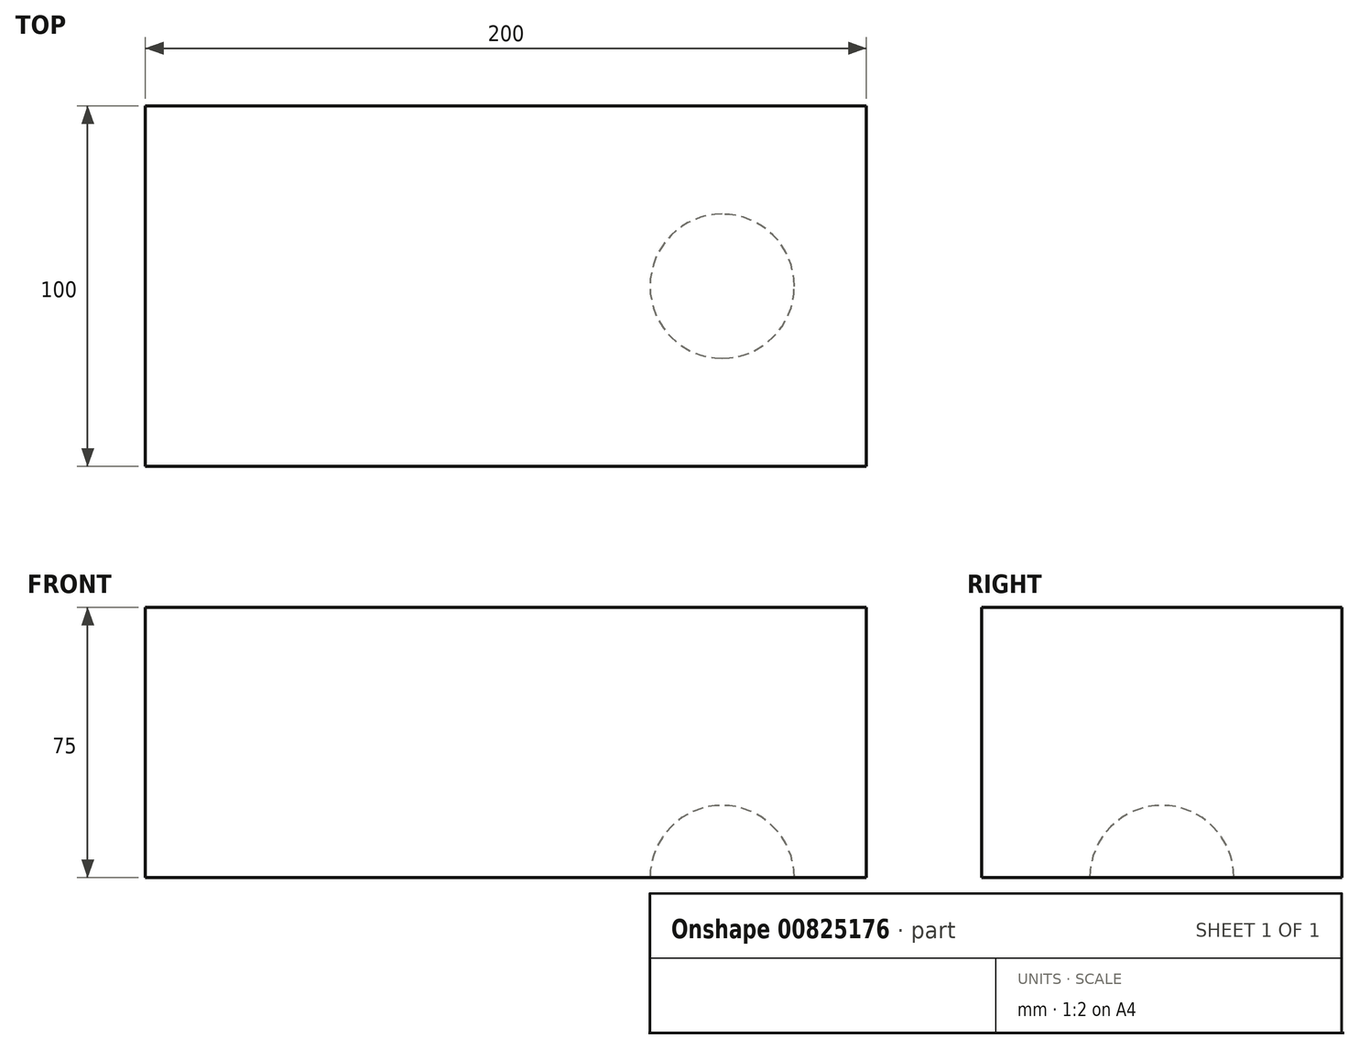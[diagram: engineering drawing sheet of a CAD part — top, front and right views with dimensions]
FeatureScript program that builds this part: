
annotation { "Feature Type Name" : "Feature", "Feature Type Description" : "" }
export const myFeature = defineFeature(function(context is Context, id is Id, definition is map)
    precondition{}
    {
        {
            var Q0;
            Q0=qCreatedBy(makeId("Top.planeOp"),FACE);
            var sketch = newSketch(context, id + "F0", { "sketchPlane" : qUnion([Q0])});
            skLineSegment(sketch, "E0.bottom", {"start": v(100, -50) * mm, "end": v(-100, -50) * mm});
            skLineSegment(sketch, "E0.top", {"start": v(100, 50) * mm, "end": v(-100, 50) * mm});
            skLineSegment(sketch, "E0.left", {"start": v(100, -50) * mm, "end": v(100, 50) * mm});
            skLineSegment(sketch, "E0.right", {"start": v(-100, -50) * mm, "end": v(-100, 50) * mm});
            skPoint(sketch, "E0.middle", {"position": v(0, 0) * mm});
            skSolve(sketch);
        }
        {
            var Q0;
            Q0 = qSketchRegion(id + "F0", true);
            extrude(context, id + "F1", {"entities" : qUnion([Q0]), "depth" : 75 * mm, "offsetDistance" : 25 * mm});
        }
        {
            var Q0;
            Q0=makeQuery(id+"F1.opExtrude","CAP_FACE",FACE,{"disambiguationData":[OSD([sQuery(id+"F0.wireOp",EDGE,"E0.bottom"),sQuery(id+"F0.wireOp",EDGE,"E0.top"),sQuery(id+"F0.wireOp",EDGE,"E0.left"),sQuery(id+"F0.wireOp",EDGE,"E0.right")])],"isStart":true});
            var sketch = newSketch(context, id + "F2", { "sketchPlane" : qUnion([Q0])});
            skArc(sketch, "E1", {"start": v(60, -20) * mm, "mid": v(80, 0) * mm, "end": v(60, 20) * mm});
            skLineSegment(sketch, "E2", {"start": v(100, 0) * mm, "end": v(-100, 0) * mm, "construction": true});
            skLineSegment(sketch, "E3", {"start": v(60, 20) * mm, "end": v(60, -20) * mm});
            skSolve(sketch);
        }
        {
            var Q0;
            Q0=makeQuery(id+"F2.imprint","IMPRINT",FACE,{"disambiguationData":[TD([[makeQuery(id+"F2.imprint","IMPRINT",EDGE,{"derivedFrom":sQuery(id+"F2.wireOp",EDGE,"E1")}),1.0]])]});
            var Q1;
            Q1=sQuery(id+"F2.wireOp",EDGE,"E3");
            revolve(context, id + "F3", {"operationType" : NewBodyOperationType.REMOVE, "surfaceOperationType" : NewSurfaceOperationType.NEW, "entities" : qUnion([Q0]), "axis" : qUnion([Q1]), "revolveType" : RevolveType.FULL, "oppositeDirection" : true});
        }
    });
